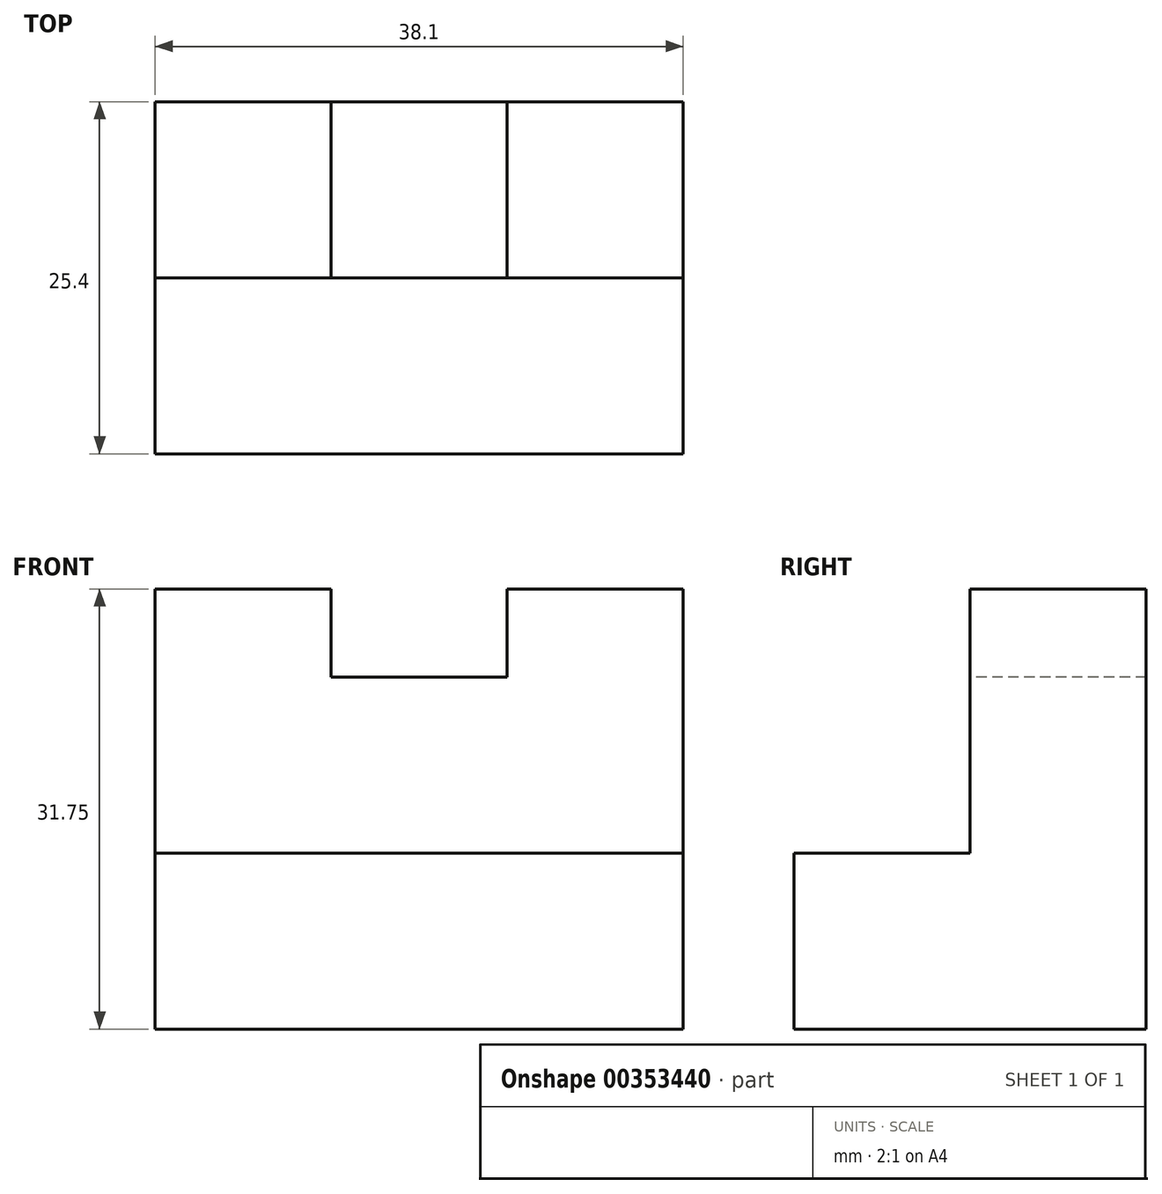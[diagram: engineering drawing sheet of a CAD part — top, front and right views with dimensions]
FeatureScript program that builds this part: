
annotation { "Feature Type Name" : "Feature", "Feature Type Description" : "" }
export const myFeature = defineFeature(function(context is Context, id is Id, definition is map)
    precondition{}
    {
        {
            var Q0;
            Q0=qCreatedBy(makeId("Right.planeOp"),FACE);
            var sketch = newSketch(context, id + "F0", { "sketchPlane" : qUnion([Q0])});
            skLineSegment(sketch, "E0", {"start": v(0, 0) * mm, "end": v(0, 12.7) * mm});
            skLineSegment(sketch, "E1", {"start": v(0, 12.7) * mm, "end": v(12.7, 12.7) * mm});
            skLineSegment(sketch, "E2", {"start": v(12.7, 12.7) * mm, "end": v(12.7, 31.75) * mm});
            skLineSegment(sketch, "E3", {"start": v(12.7, 31.75) * mm, "end": v(25.4, 31.75) * mm});
            skLineSegment(sketch, "E4", {"start": v(25.4, 31.75) * mm, "end": v(25.4, 0) * mm});
            skLineSegment(sketch, "E5", {"start": v(25.4, 0) * mm, "end": v(0, 0) * mm});
            skSolve(sketch);
        }
        {
            var Q0;
            Q0 = qSketchRegion(id + "F0", true);
            extrude(context, id + "F1", {"entities" : qUnion([Q0]), "oppositeDirection" : true, "depth" : 38.1 * mm});
        }
        {
            var Q0;
            Q0=makeQuery(id+"F1.opExtrude","SWEPT_FACE",FACE,{"disambiguationData":[OSD([sQuery(id+"F0.wireOp",EDGE,"E3")])]});
            var sketch = newSketch(context, id + "F2", { "sketchPlane" : qUnion([Q0])});
            skLineSegment(sketch, "E6", {"start": v(-25.4, 25.4) * mm, "end": v(-25.4, 12.7) * mm});
            skLineSegment(sketch, "E7", {"start": v(-25.4, 12.7) * mm, "end": v(-12.7, 12.7) * mm});
            skLineSegment(sketch, "E8", {"start": v(-12.7, 12.7) * mm, "end": v(-12.7, 25.4) * mm});
            skLineSegment(sketch, "E9", {"start": v(-12.7, 25.4) * mm, "end": v(-25.4, 25.4) * mm});
            skSolve(sketch);
        }
        {
            var Q0;
            Q0 = qSketchRegion(id + "F2", true);
            extrude(context, id + "F3", {"entities" : qUnion([Q0]), "operationType" : NewBodyOperationType.REMOVE, "oppositeDirection" : true, "depth" : 6.35 * mm});
        }
    });
